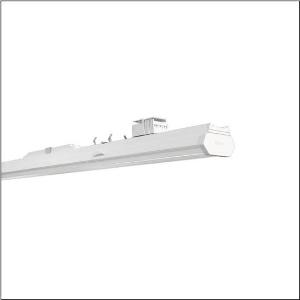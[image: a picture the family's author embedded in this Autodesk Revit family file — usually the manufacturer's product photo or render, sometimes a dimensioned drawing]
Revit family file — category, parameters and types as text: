
# Revit family: licross_r__11_protected_mo_51td1bdn49xg_f089
name_source: partatom
category: Lighting Fixtures
units: mm (PartAtom-declared; Revit-internal decimal feet)

## family parameters
Cut with Voids When Loaded = No
Host = Face
Light Source = No
Part Type = Normal
Room Calculation Point = No
Round Connector Dimension = Use Diameter
Shared = No

## types (1)
- --- (1 x LED, 9370 lm, 57.1 W, 4000K)
    Apparent Load = 57 VA
    CIE Flux Codes = 54 82 95 97 100
    Color Rendering = 80
    Color Temperature = 4000K
    Default Elevation = 1800 mm
    Description = Licross® 11 Protected MO, luminaire insert, of sheet steel, galvanised, coil coated, white, length: 1.500mm, width: 90mm, height: 101mm, LED rated luminous flux: 9.370lm, light colour: 840, SDCM (Standard Deviation of Colour Matching)MacAdam ≤ 2 SDCM (initial), control gear: DALI 2, with plug, 5-pole, with phase selection, mains connection: 220..240V, AC, 50/60Hz, rated input power: 57W, internal wiring halogen-free, primary optical cover: cover, of PMMA, light emission: direct distribution, primary light characteristic: symmetric, protection rating (complete): IP54, insulation class (complete): insulation class I (protective earthing), certification: CE, ENEC, VDE, UKCA, protection symbol: D if used in an environment with non-conductive dust loads with corresponding accessories, impact resistance: IK06, permissible ambient temperature for indoor applications: -25..+35°C, corresponds to IFS (International Featured Standards) requirements for safety and quality in the food industry, reducing of maximum allowable ambient temperature of 5°C with ceiling mounting, LABS conformity tested according to VDMA 24364:2018-05, packaging unit: 1 piece
    Height = 92 mm
    Lamp = 1 x LED
    Lamp Light Flux = 9370 lm
    Lamp Power = 57.1 W
    Lamp count = 1
    Length = 1500 mm
    Luminous efficacy = 164 lm/W
    Manufacturer = Siteco
    ModVariant = No
    Model = 51TD1BDN49XG
    Mounting Place = Ceiling
    Mounting Type = Pendant
    Number of Poles = 1
    OnlyDefault = Yes
    Power Factor = 1
    Product Name = Licross® 11 Protected MO
    Product group = luminaire insert | ceiling pendant
    ProductGroupID = 901
    Protection Class = Protection class I
    Protection Degree = IP 54
    RLX_Detail_Level = 1
    RLX_Emergency_Light_Flux = 0 lm
    RLX_Emergency_Type = 0
    RLX_Emergency_Type_DB = No
    RlxData = <blob elided: 24545 chars, md5=616f4e01>
    Socket = socket
    Standby Power = 0 W
    System Light Flux = 9370 lm
    System Power = 57 W
    Type Comments = factory setting: luminous flux: 100 % | dim-lin: 254 | 378 mA
    Type Image = l_1256145.jpg
    URL = http://relux.com
    VarID = @adj_106767
    Voltage = 0 V
    Weight = 0.00 kg
    Width = 88 mm

## geometry (parser evidence)
native form markers: Blend x4, Sweep x10
no freeform markers — native parametric forms only
